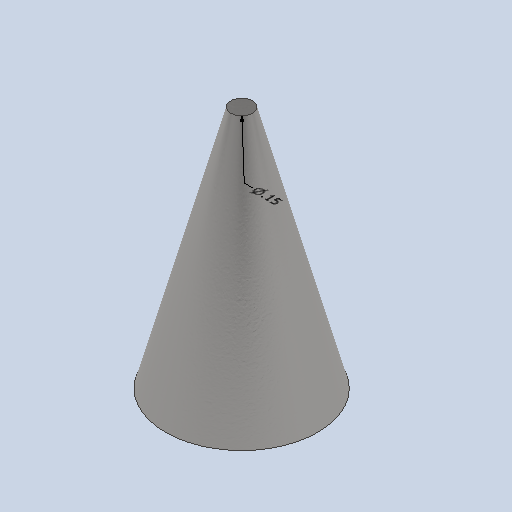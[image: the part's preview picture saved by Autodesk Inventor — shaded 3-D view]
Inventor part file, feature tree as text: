
AUTODESK INVENTOR PART (.ipt)
format: ipt  version: 2022 (Build 260153000, 153)  size: 158,720 bytes
history: native  units: in
note: dims shown in document units (in); Inventor stores cm internally (conversion verified against a paired STEP export)
features: other x2, sketch x2, revolve x1, shell x1, extrude x1
ambient origin geometry x8: Origin, YZ Plane, XZ Plane, XY Plane, X Axis, Y Axis, Z Axis, Center Point
bodies: Solid1 (feature_tree)
feature tree (7):
  other  "Annotations"
  revolve  "Revolution1"  Angle=75.0deg
  shell  "Shell1"  Thickness=1.633in
  extrude  "Extrusion1"  Depth=0.0709in
  sketch  "Sketch1"  dims[d0=0.05in d1=75.0deg d2=1.633in]
  sketch  "Sketch2"  dims[d3=90.0deg d4=0.0312in d7=0.0709in d8=0.25in d9=1.0in d10=0.0in d5=0.9353in d6=0.148in]
  other  "Diameter Dimension 1"
